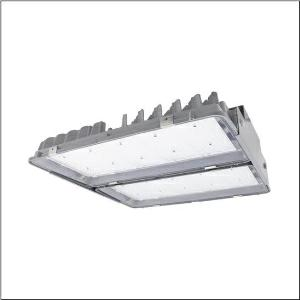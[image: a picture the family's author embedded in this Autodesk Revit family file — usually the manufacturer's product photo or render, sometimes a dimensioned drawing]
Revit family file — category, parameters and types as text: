
# Revit family: highbay_11xtreme_51hf81db4wma
name_source: partatom
category: Lighting Fixtures
units: mm (PartAtom-declared; Revit-internal decimal feet)

## family parameters
Cut with Voids When Loaded = No
Host = Face
Light Source = No
Part Type = Normal
Room Calculation Point = No
Round Connector Dimension = Use Diameter
Shared = No

## types (1)
- --- (1 x LED, 76000 lm, 422.2 W, 4000K)
    Apparent Load = 422 VA
    CIE Flux Codes = 88 96 99 100 100
    Color Rendering = 80
    Color Temperature = 4000K
    Default Elevation = 1800 mm
    Description = Highbay 11Xtreme, LED high bay luminaire, primary light control with lens, of PMMA, primary optical cover: cover, of toughened safety glass, light emission: direct distribution, primary light characteristic: symmetric, installation type: suspended mounting, surface-mounted, 2x LED module,for 1x 2x LED, rated luminous flux: 76.000lm, luminous efficacy: 180lm/W, light colour: 840, colour temperature: 4000K, with cable H07RN-F 5x 1.5mm², mains connection: 220..240V, AC, 50/60Hz, cable length: 1,5m, rated input power: 422W, luminaire housing, of diecast aluminium, partly coated, silver, length: 595mm, width: 560mm, height: 195mm, protection rating (complete): IP66, insulation class (complete): insulation class I (protective earthing), certification: CE, ENEC, UKCA, protection symbol: D, ball protection: ball impact resistant according to DIN VDE 0710 part 13 (with chain suspension), impact resistance: IK08, permissible operating ambient temperature: -25..+45°C, reducing of maximum allowable ambient temperature of 5°C with ceiling mounting, packaging unit: 1 piece
    Height = 157 mm
    Lamp = 1 x LED
    Lamp Light Flux = 76000 lm
    Lamp Power = 422.2 W
    Lamp count = 1
    Length = 593 mm
    Luminous efficacy = 180 lm/W
    Manufacturer = Siteco
    ModVariant = No
    Model = 51HF81DB4WMA
    Mounting Place = Ceiling
    Mounting Type = Pendant
    Number of Poles = 1
    OnlyDefault = Yes
    Power Factor = 1
    Product Name = Highbay 11Xtreme
    Product group = LED high bay luminaire
    ProductGroupID = 903
    Protection Class = Protection class I
    Protection Degree = IP 66
    RLX_Detail_Level = 1
    RLX_Emergency_Light_Flux = 0 lm
    RLX_Emergency_Type = 0
    RLX_Emergency_Type_DB = No
    RlxData = <blob elided: 33845 chars, md5=1f6ae33e>
    Socket = socket
    Standby Power = 0 W
    System Light Flux = 76000 lm
    System Power = 422 W
    Type Comments = factory setting: luminous flux: 100 % | dim-lin: 254 | 1389 mA
    Type Image = l_1258340.jpg
    URL = http://relux.com
    VarID = @adj_035923
    Voltage = 0 V
    Weight = 0.00 kg
    Width = 278 mm

## geometry (parser evidence)
native form markers: Blend x4, Sweep x11
no freeform markers — native parametric forms only
